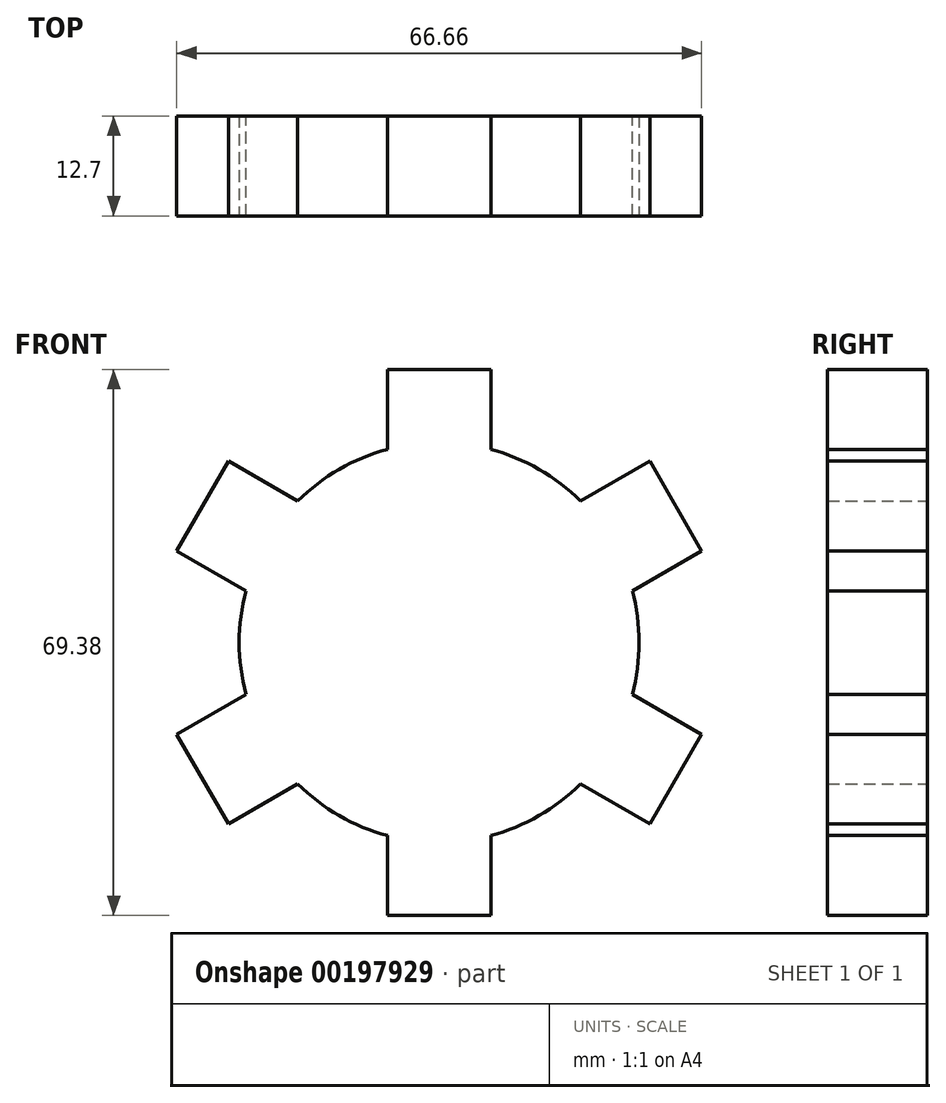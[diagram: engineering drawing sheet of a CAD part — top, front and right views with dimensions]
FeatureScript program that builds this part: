
annotation { "Feature Type Name" : "Feature", "Feature Type Description" : "" }
export const myFeature = defineFeature(function(context is Context, id is Id, definition is map)
    precondition{}
    {
        {
            var Q0;
            Q0=qCreatedBy(makeId("Front.planeOp"),FACE);
            var sketch = newSketch(context, id + "F0", { "sketchPlane" : qUnion([Q0])});
            skCircle(sketch, "E0", {"center": v(0, 0) * mm, "radius": 25.4 * mm});
            skSolve(sketch);
        }
        {
            var Q0;
            Q0 = qSketchRegion(id + "F0", true);
            extrude(context, id + "F1", {"entities" : qUnion([Q0]), "endBound" : BoundingType.SYMMETRIC, "oppositeDirection" : true, "depth" : 12.7 * mm});
        }
        {
            var Q0;
            Q0=makeQuery(id+"F1.opExtrude","CAP_FACE",FACE,{"disambiguationData":[OSD([sQuery(id+"F0.wireOp",EDGE,"E0")])],"isStart":false});
            var sketch = newSketch(context, id + "F2", { "sketchPlane" : qUnion([Q0])});
            skLineSegment(sketch, "E1", {"start": v(0, 0) * mm, "end": v(6.57, -24.53) * mm});
            skLineSegment(sketch, "E2", {"start": v(0, 0) * mm, "end": v(-6.57, -24.53) * mm});
            skLineSegment(sketch, "E3", {"start": v(0, 0) * mm, "end": v(0, -25.4) * mm});
            skLineSegment(sketch, "E4", {"start": v(-6.57, -24.53) * mm, "end": v(6.57, -24.53) * mm});
            skLineSegment(sketch, "E5.0", {"start": v(-6.57, -34.7) * mm, "end": v(6.57, -34.7) * mm});
            skLineSegment(sketch, "E6", {"start": v(-6.57, -34.7) * mm, "end": v(-6.57, -24.53) * mm});
            skLineSegment(sketch, "E7", {"start": v(6.57, -34.7) * mm, "end": v(6.57, -24.53) * mm});
            skSolve(sketch);
        }
        {
            var Q0;
            Q0 = qSketchRegion(id + "F2", true);
            var Q1;
            {var subQ0=sQuery(id+"F2.wireOp",EDGE,"E1");Q1=makeQuery(id+"F2.imprint","IMPRINT",FACE,{"disambiguationData":[TD([[makeQuery(id+"F2.imprint","IMPRINT",EDGE,{"derivedFrom":subQ0}),1.0]])]});}
            extrude(context, id + "F3", {"entities" : qUnion([Q0, Q1]), "operationType" : NewBodyOperationType.ADD, "oppositeDirection" : true, "depth" : 12.7 * mm});
        }
        {
            var Q0;
            Q0=qCreatedBy(makeId("Top.planeOp"),FACE);
            var sketch = newSketch(context, id + "F4", { "sketchPlane" : qUnion([Q0])});
            skLineSegment(sketch, "E8", {"start": v(0, 0) * mm, "end": v(0, -48.96) * mm});
            skSolve(sketch);
        }
        {
            var Q0;
            Q0=makeQuery(id+"F1.opExtrude","SWEPT_BODY",BODY,{"disambiguationData":[OSD([sQuery(id+"F0.wireOp",EDGE,"E0")])]});
            var Q1;
            Q1=sQuery(id+"F4.wireOp",EDGE,"E8");
            circularPattern(context, id + "F5", {"operationType" : NewBodyOperationType.ADD, "entities" : qUnion([Q0]), "axis" : qUnion([Q1]), "angle" : 360 * degree, "instanceCount" : 6, "equalSpace" : true});
        }
    });
